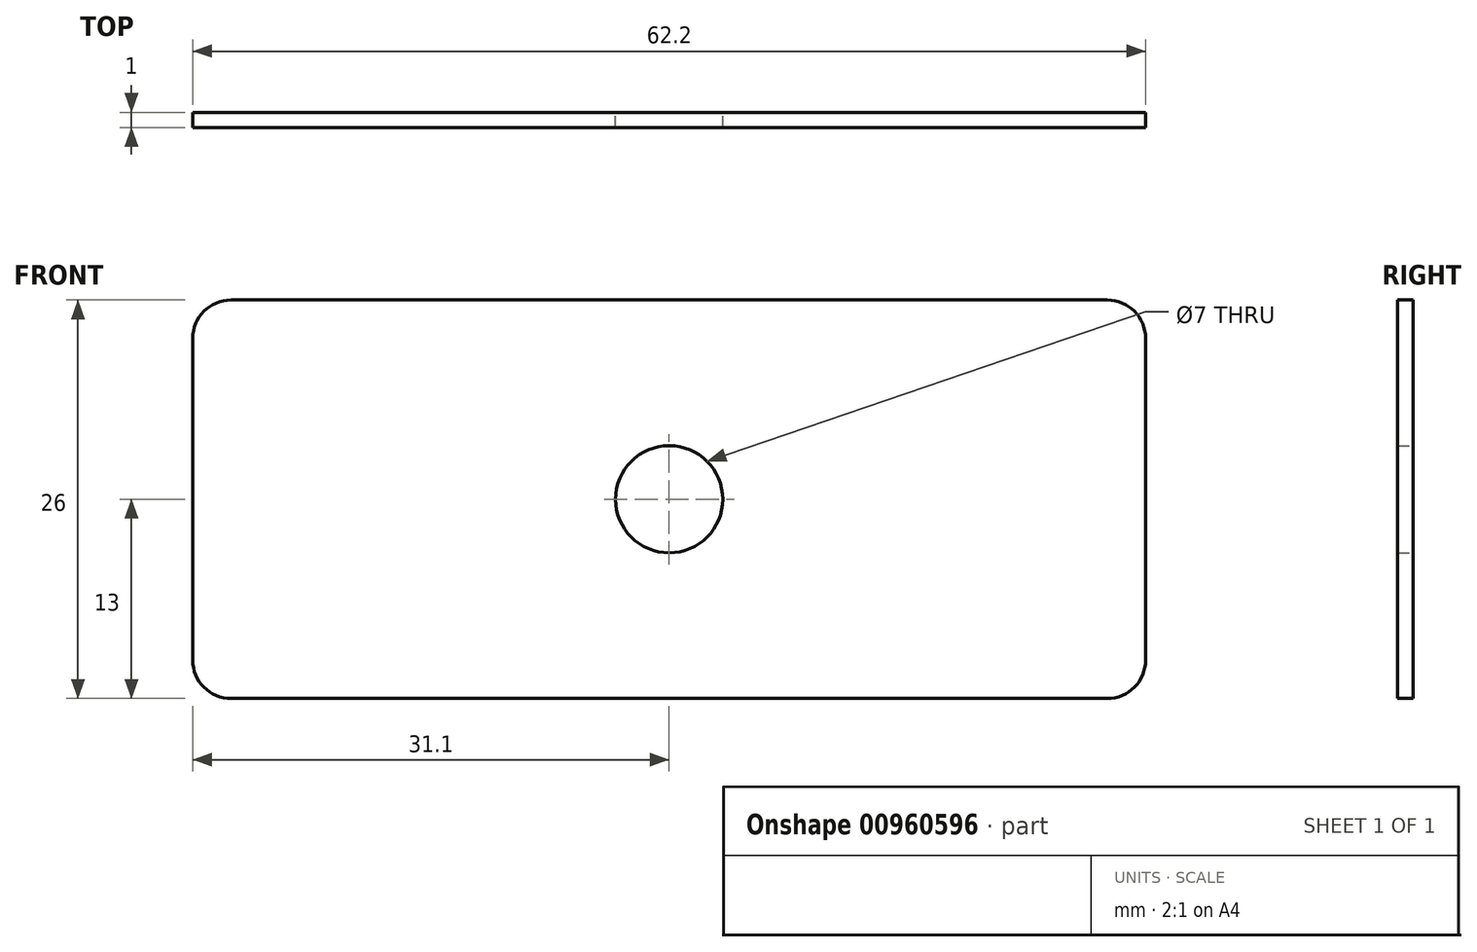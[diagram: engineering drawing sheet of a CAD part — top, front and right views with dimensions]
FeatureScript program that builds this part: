
annotation { "Feature Type Name" : "Feature", "Feature Type Description" : "" }
export const myFeature = defineFeature(function(context is Context, id is Id, definition is map)
    precondition{}
    {
        {
            var Q0;
            Q0=qCreatedBy(makeId("Front.planeOp"),FACE);
            var sketch = newSketch(context, id + "F0", { "sketchPlane" : qUnion([Q0])});
            skLineSegment(sketch, "E0.bottom", {"start": v(-28.6, 13) * mm, "end": v(28.6, 13) * mm});
            skLineSegment(sketch, "E0.top", {"start": v(-28.6, -13) * mm, "end": v(28.6, -13) * mm});
            skLineSegment(sketch, "E0.left", {"start": v(-31.1, 10.5) * mm, "end": v(-31.1, -10.5) * mm});
            skLineSegment(sketch, "E0.right", {"start": v(31.1, 10.5) * mm, "end": v(31.1, -10.5) * mm});
            skPoint(sketch, "E0.middle", {"position": v(0, 0) * mm});
            skCircle(sketch, "E1", {"center": v(0, 0) * mm, "radius": 3.5 * mm});
            skPoint(sketch, "E2.visualSharp", {"position": v(-31.1, 13) * mm});
            skArc(sketch, "E2.filletArc", {"start": v(-28.6, 13) * mm, "mid": v(-30.37, 12.27) * mm, "end": v(-31.1, 10.5) * mm});
            skPoint(sketch, "E3.visualSharp", {"position": v(-31.1, -13) * mm});
            skArc(sketch, "E3.filletArc", {"start": v(-31.1, -10.5) * mm, "mid": v(-30.37, -12.27) * mm, "end": v(-28.6, -13) * mm});
            skPoint(sketch, "E4.visualSharp", {"position": v(31.1, -13) * mm});
            skArc(sketch, "E4.filletArc", {"start": v(28.6, -13) * mm, "mid": v(30.37, -12.27) * mm, "end": v(31.1, -10.5) * mm});
            skPoint(sketch, "E5.visualSharp", {"position": v(31.1, 13) * mm});
            skArc(sketch, "E5.filletArc", {"start": v(31.1, 10.5) * mm, "mid": v(30.37, 12.27) * mm, "end": v(28.6, 13) * mm});
            skSolve(sketch);
        }
        {
            var Q0;
            Q0=makeQuery(id+"F0.imprint","IMPRINT",FACE,{"disambiguationData":[TD([[makeQuery(id+"F0.imprint","IMPRINT",EDGE,{"derivedFrom":sQuery(id+"F0.wireOp",EDGE,"E0.bottom")}),-1.0]])]});
            extrude(context, id + "F1", {"entities" : qUnion([Q0]), "depth" : 1 * mm, "offsetDistance" : 25 * mm});
        }
    });
